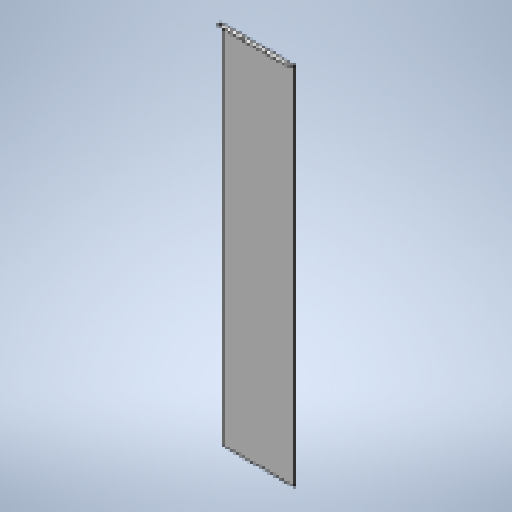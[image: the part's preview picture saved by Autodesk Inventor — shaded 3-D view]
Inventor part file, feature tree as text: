
AUTODESK INVENTOR PART (.ipt)
format: ipt  version: 2025 (Build 290162010, 162A)  size: 197,120 bytes
history: native  units: mm
features: sheet_metal_op x4, sketch x3, other x3, chamfer x1, projected_geometry x1
ambient origin geometry x8: Origin, YZ Plane, XZ Plane, XY Plane, X Axis, Y Axis, Z Axis, Center Point
bodies: Solid1 (feature_tree)
feature tree (12):
  sheet_metal_op  "Face1"
  sheet_metal_op  "Flange2"
  chamfer  "Corner Round1"
  sketch  "Sketch1"  dims[d0=2011.081mm]
  other  "Plate1"
  sketch  "Sketch4"  dims[d1=400.0mm]
  other  "Plate3"
  sheet_metal_op  "Bend2"
  sheet_metal_op  "Corner2"
  sketch  "Sketch8"  dims[d2=2.0mm d16=2.0mm d17=1.0mm d18=4.0mm d19=2.75mm d20=30.0mm d21=14.835299mm d22=2.75mm d23=8.0mm d24=2.0mm d25=2.75mm d33=140.0mm d34=380.0mm d35=5.0mm d36=2.0mm d37=0.0mm d38=6.0mm]
  projected_geometry  "Projected Loop3"
  other  "Cut1"
